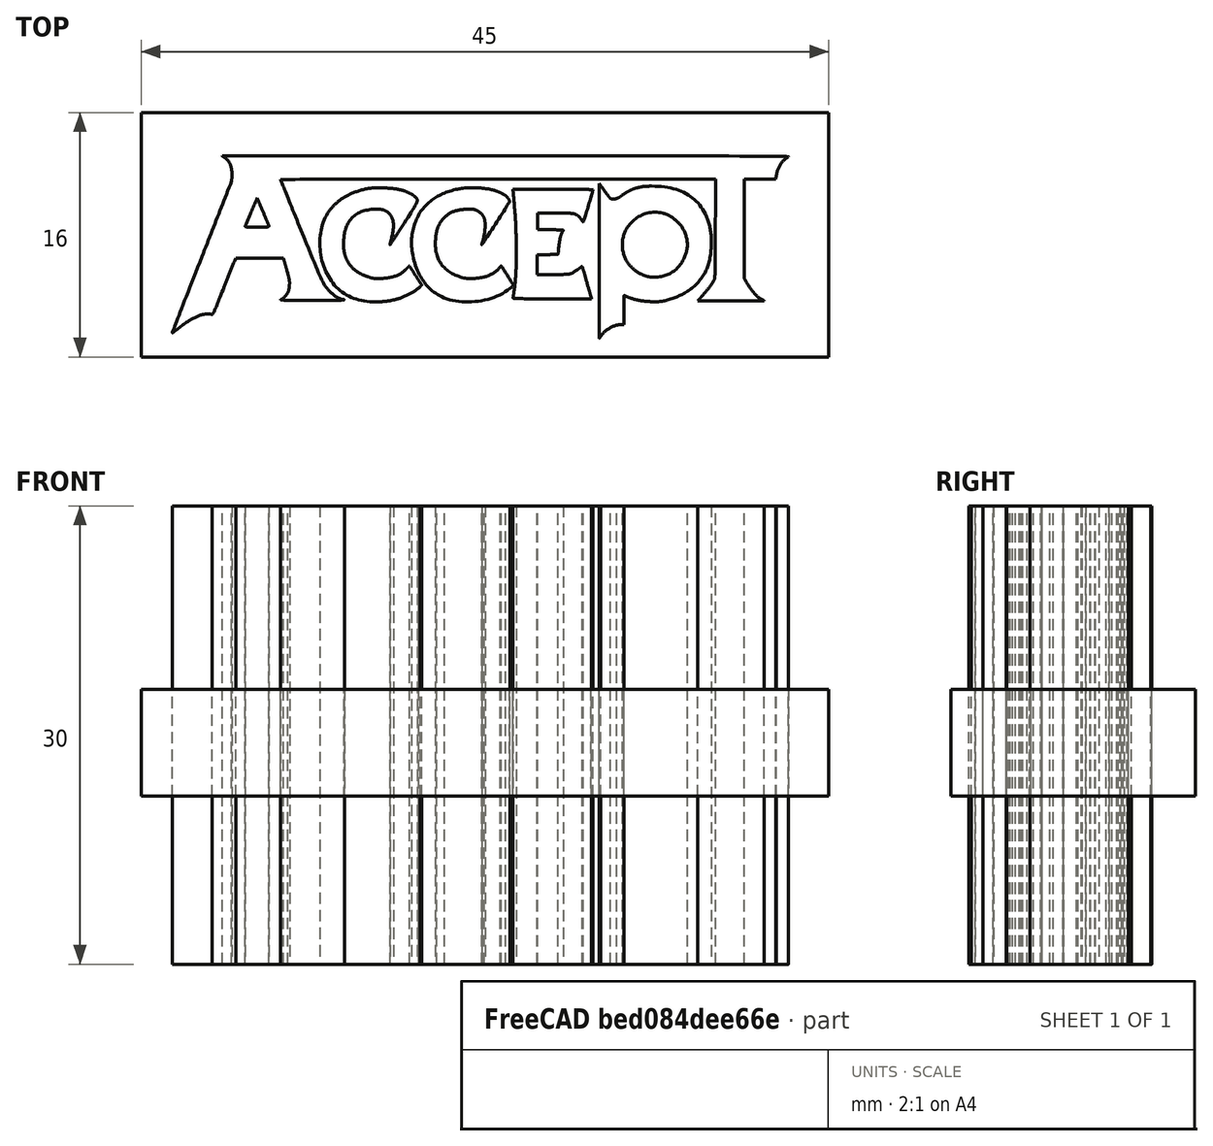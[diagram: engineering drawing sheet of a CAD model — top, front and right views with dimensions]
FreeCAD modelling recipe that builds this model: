
FCSTD DOCUMENT  (FreeCAD 0.18R16131 (Git))
Label: 12
License: All rights reserved
LicenseURL: http://en.wikipedia.org/wiki/All_rights_reserved
objects: Part::Feature×7, Part::Extrusion×7, Part::Cut×2, Part::FeaturePython×1, Part::Box×1
note: 18 computed .brp shape members not serialized (recipe doc carries the construction recipe); baked Part::Feature solids carry a one-line shape summary decoded from their .brp

FEATURE [Part::Feature] Path
  shape: bbox 404.3 x 115.9 x 2e-07 mm, 0 faces, 0 solids (baked)
FEATURE [Part::Feature] Path001
  shape: bbox 16.02 x 18.98 x 2e-07 mm, 0 faces, 0 solids (baked)
FEATURE [Part::Feature] Path002
  shape: bbox 73.8 x 101.8 x 2e-07 mm, 0 faces, 0 solids (baked)
FEATURE [Part::Feature] Path003
  shape: bbox 43.39 x 43.37 x 2e-07 mm, 0 faces, 0 solids (baked)
FEATURE [Part::Feature] Path004
  shape: bbox 67.64 x 75.67 x 2e-07 mm, 0 faces, 0 solids (baked)
FEATURE [Part::Feature] Path005
  shape: bbox 67.17 x 76.29 x 2e-07 mm, 0 faces, 0 solids (baked)
FEATURE [Part::Feature] Path006
  shape: bbox 52.63 x 71.61 x 2e-07 mm, 0 faces, 0 solids (baked)
FEATURE [Part::Extrusion] Extrude
  Base = -> Path004
  Dir = (0,0,1)
  DirMode = 2
  FaceMakerClass = Part::FaceMakerBullseye
  LengthFwd = 10
  LengthRev = 0
  Solid = true
  Symmetric = false
FEATURE [Part::Extrusion] Extrude001
  Base = -> Path006
  Dir = (0,0,1)
  DirMode = 2
  FaceMakerClass = Part::FaceMakerBullseye
  LengthFwd = 10
  LengthRev = 0
  Solid = true
  Symmetric = false
FEATURE [Part::Extrusion] Extrude002
  Base = -> Path005
  Dir = (0,0,1)
  DirMode = 2
  FaceMakerClass = Part::FaceMakerBullseye
  LengthFwd = 10
  LengthRev = 0
  Solid = true
  Symmetric = false
FEATURE [Part::Extrusion] Extrude003
  Base = -> Path002
  Dir = (0,0,1)
  DirMode = 2
  FaceMakerClass = Part::FaceMakerBullseye
  LengthFwd = 10
  LengthRev = 0
  Solid = true
  Symmetric = false
FEATURE [Part::Extrusion] Extrude004
  Base = -> Path003
  Dir = (0,0,-1)
  DirMode = 2
  FaceMakerClass = Part::FaceMakerBullseye
  LengthFwd = 10
  LengthRev = 0
  Placement = pos=(0,0,10) rot=(0,0,1;0rad)
  Solid = true
  Symmetric = false
FEATURE [Part::Cut] Cut
  Base = -> Extrude003
  Tool = -> Extrude004
FEATURE [Part::Extrusion] Extrude005
  Base = -> Path
  Dir = (0,0,1)
  DirMode = 2
  FaceMakerClass = Part::FaceMakerBullseye
  LengthFwd = 10
  LengthRev = 0
  Solid = true
  Symmetric = false
FEATURE [Part::Extrusion] Extrude006
  Base = -> Path001
  Dir = (0,0,-1)
  DirMode = 2
  FaceMakerClass = Part::FaceMakerBullseye
  LengthFwd = 10
  LengthRev = 0
  Placement = pos=(0,0,10) rot=(0,0,1;0rad)
  Solid = true
  Symmetric = false
FEATURE [Part::Cut] Cut001
  Base = -> Extrude005
  Tool = -> Extrude006
FEATURE [Part::FeaturePython] Scale  # Draft clone (typed FeaturePython)
  Fuse = false
  Objects = -> [Extrude,Extrude001,Extrude002,Cut,Cut001]
  Scale = (0.1,0.1,3)
FEATURE [Part::Box] Box  label="Куб"
  AttacherType = Attacher::AttachEngine3D
  Height = 7
  Length = 45
  Placement = pos=(-2,0,11) rot=(0,0,1;0rad)
  Width = 16
